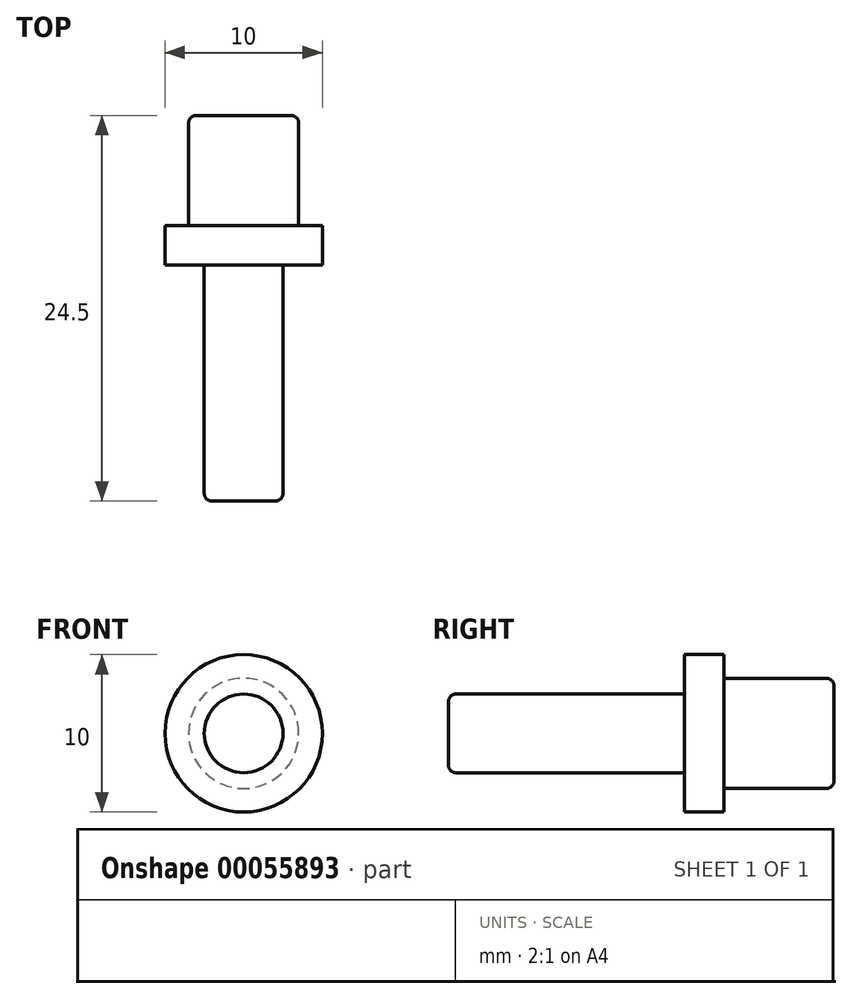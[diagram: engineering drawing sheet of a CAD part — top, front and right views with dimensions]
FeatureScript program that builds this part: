
annotation { "Feature Type Name" : "Feature", "Feature Type Description" : "" }
export const myFeature = defineFeature(function(context is Context, id is Id, definition is map)
    precondition{}
    {
        {
            var Q0;
            Q0=qCreatedBy(makeId("Front.planeOp"),FACE);
            var sketch = newSketch(context, id + "F0", { "sketchPlane" : qUnion([Q0])});
            skCircle(sketch, "E0", {"center": v(0, 0) * mm, "radius": 2.5 * mm});
            skCircle(sketch, "E1", {"center": v(0, 0) * mm, "radius": 5 * mm});
            skCircle(sketch, "E2", {"center": v(0, 0) * mm, "radius": 3.5 * mm});
            skSolve(sketch);
        }
        {
            var Q0;
            Q0=makeQuery(id+"F0.imprint","IMPRINT",FACE,{"disambiguationData":[TD([[makeQuery(id+"F0.imprint","IMPRINT",EDGE,{"derivedFrom":sQuery(id+"F0.wireOp",EDGE,"E0")}),1.0]])]});
            extrude(context, id + "F1", {"entities" : qUnion([Q0]), "depth" : 15 * mm});
        }
        {
            var Q0;
            Q0=makeQuery(id+"F0.imprint","IMPRINT",FACE,{"disambiguationData":[TD([[makeQuery(id+"F0.imprint","IMPRINT",EDGE,{"derivedFrom":sQuery(id+"F0.wireOp",EDGE,"E1")}),1.0]])]});
            var Q1;
            Q1=makeQuery(id+"F0.imprint","IMPRINT",FACE,{"disambiguationData":[TD([[makeQuery(id+"F0.imprint","IMPRINT",EDGE,{"derivedFrom":sQuery(id+"F0.wireOp",EDGE,"E0")}),-1.0]])]});
            var Q2;
            Q2=makeQuery(id+"F0.imprint","IMPRINT",FACE,{"disambiguationData":[TD([[makeQuery(id+"F0.imprint","IMPRINT",EDGE,{"derivedFrom":sQuery(id+"F0.wireOp",EDGE,"E0")}),1.0]])]});
            extrude(context, id + "F2", {"entities" : qUnion([Q0, Q1, Q2]), "operationType" : NewBodyOperationType.ADD, "oppositeDirection" : true, "depth" : 2.5 * mm});
        }
        {
            var Q0;
            Q0=makeQuery(id+"F0.imprint","IMPRINT",FACE,{"disambiguationData":[TD([[makeQuery(id+"F0.imprint","IMPRINT",EDGE,{"derivedFrom":sQuery(id+"F0.wireOp",EDGE,"E0")}),-1.0]])]});
            var Q1;
            Q1=makeQuery(id+"F0.imprint","IMPRINT",FACE,{"disambiguationData":[TD([[makeQuery(id+"F0.imprint","IMPRINT",EDGE,{"derivedFrom":sQuery(id+"F0.wireOp",EDGE,"E0")}),1.0]])]});
            extrude(context, id + "F3", {"entities" : qUnion([Q0, Q1]), "operationType" : NewBodyOperationType.ADD, "oppositeDirection" : true, "depth" : 9.5 * mm});
        }
        {
            var Q0;
            Q0=makeQuery(id+"F3.opExtrude","CAP_EDGE",EDGE,{"disambiguationData":[OSD([sQuery(id+"F0.wireOp",EDGE,"E2")])],"isStart":false});
            fillet(context, id + "F4", {"entities" : qUnion([Q0]), "radius" : 0.5 * mm, "tangentPropagation" : true, "allowEdgeOverflow" : false});
        }
        {
            var Q0;
            Q0=makeQuery(id+"F1.opExtrude","CAP_EDGE",EDGE,{"disambiguationData":[OSD([sQuery(id+"F0.wireOp",EDGE,"E0")])],"isStart":false});
            fillet(context, id + "F5", {"entities" : qUnion([Q0]), "radius" : 0.5 * mm, "tangentPropagation" : true, "allowEdgeOverflow" : false});
        }
    });
